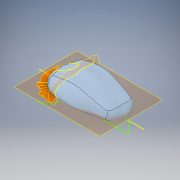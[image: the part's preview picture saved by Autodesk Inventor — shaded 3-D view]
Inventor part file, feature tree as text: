
AUTODESK INVENTOR PART (.ipt)
format: ipt  version: 2019 (Build 230136000, 136)  size: 1,594,368 bytes
history: native  units: mm
features: other x13, sketch x5, split x3, surface_op x2, plane x1
ambient origin geometry x8: Origin, YZ Plane, XZ Plane, XY Plane, X Axis, Y Axis, Z Axis, Center Point
bodies: Solid1 (feature_tree)
feature tree (24):
  other  "CrossSection1"
  other  "Curvature1"
  sketch  "Sketch1"  dims[d1=120.0mm]
  sketch  "Sketch2"  dims[d5=60.0mm]
  other  "Form1"
  sketch  "Sketch3"  dims[d6=7.0mm]
  sketch  "Sketch4"  dims[d8=120.0mm d12=60.0mm d13=42.0mm d14=0.5mm d15=2.0mm d16=0.0mm d17=20.0mm d19=8.0mm d20=3.0mm d21=3.0mm d22=10.0mm d23=0.0mm d24=3.0mm d25=10.0mm d26=0.0mm d27=3.0mm]
  sketch  "3D Sketch1"
  split  "Split1"
  split  "Split2"
  plane  "Work Plane1"
  split  "Split3"
  other  "Ruled Surface1"
  surface_op  "Extend1"
  other  "Ruled Surface2"
  surface_op  "Extend2"
  other  "Image1"
  other  "Image2"
  other  "Project to Surface1"
  other  "Project to Surface2"
  other  "Srf1"
  other  "Srf2"
  other  "Srf3"
  other  "OffsetSrf1"
